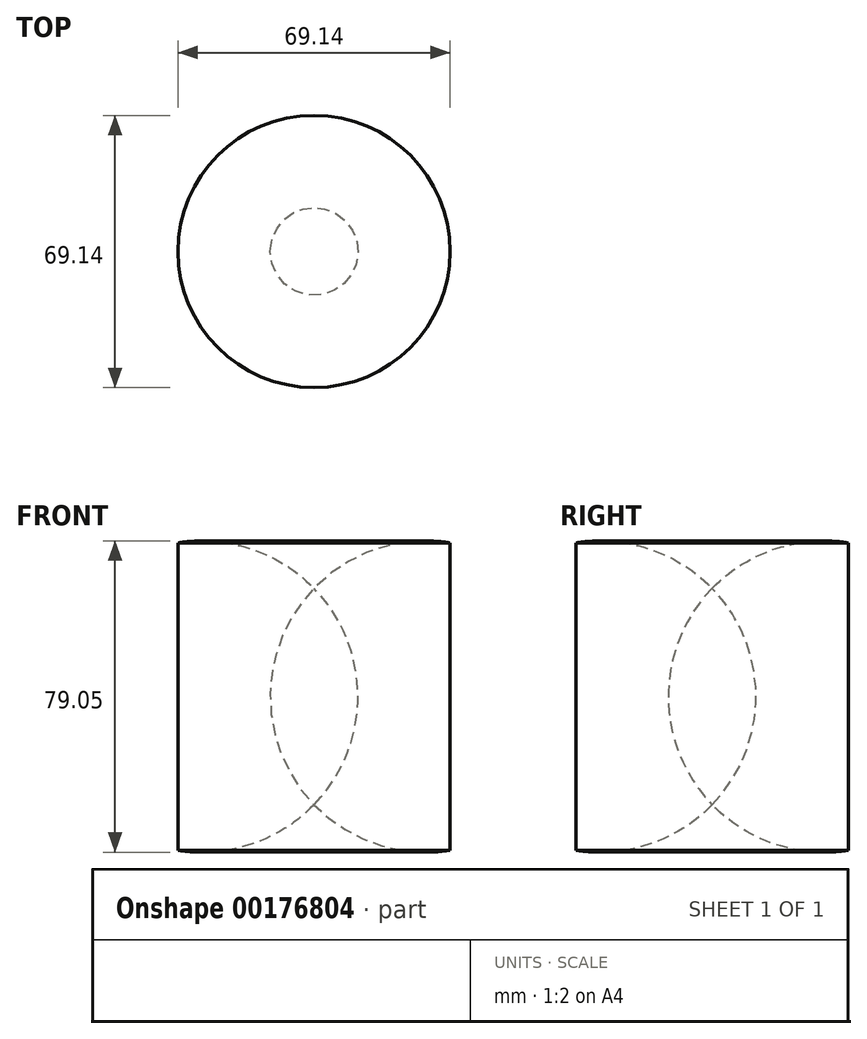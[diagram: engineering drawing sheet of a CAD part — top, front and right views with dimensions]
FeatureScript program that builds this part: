
annotation { "Feature Type Name" : "Feature", "Feature Type Description" : "" }
export const myFeature = defineFeature(function(context is Context, id is Id, definition is map)
    precondition{}
    {
        {
            var Q0;
            Q0=qCreatedBy(makeId("Front.planeOp"),FACE);
            var sketch = newSketch(context, id + "F0", { "sketchPlane" : qUnion([Q0])});
            skLineSegment(sketch, "E0", {"start": v(-50.5, 57.06) * mm, "end": v(-50.5, -24.29) * mm});
            skLineSegment(sketch, "E1", {"start": v(-15.94, 55.87) * mm, "end": v(-15.94, -22.2) * mm});
            skArc(sketch, "E2", {"start": v(-15.94, -22.2) * mm, "mid": v(17.4, 16.84) * mm, "end": v(-15.94, 55.87) * mm});
            skSolve(sketch);
        }
        {
            var Q0;
            Q0=makeQuery(id+"F0.imprint","IMPRINT",FACE,{"disambiguationData":[TD([[makeQuery(id+"F0.imprint","IMPRINT",EDGE,{"derivedFrom":sQuery(id+"F0.wireOp",EDGE,"E1")}),1.0]])]});
            var Q1;
            Q1=sQuery(id+"F0.wireOp",EDGE,"E0");
            revolve(context, id + "F1", {"entities" : qUnion([Q0]), "axis" : qUnion([Q1]), "revolveType" : RevolveType.FULL});
        }
    });
